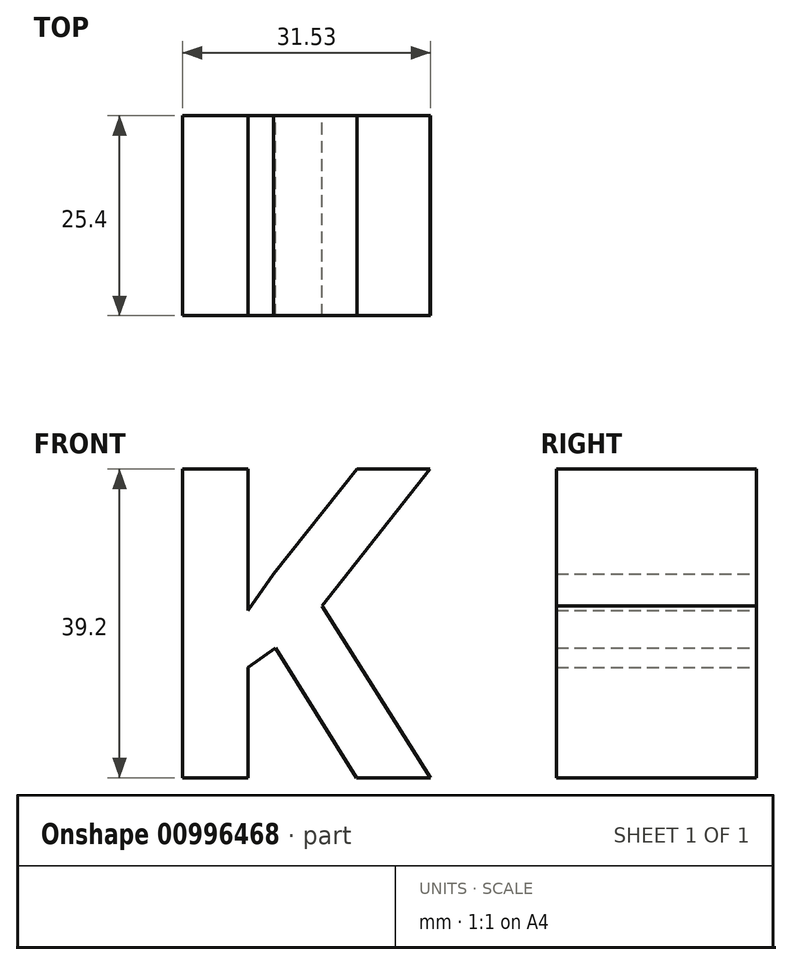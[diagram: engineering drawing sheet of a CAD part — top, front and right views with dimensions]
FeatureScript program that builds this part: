
annotation { "Feature Type Name" : "Feature", "Feature Type Description" : "" }
export const myFeature = defineFeature(function(context is Context, id is Id, definition is map)
    precondition{}
    {
        {
            var Q0;
            Q0=qCreatedBy(makeId("Front.planeOp"),FACE);
            var sketch = newSketch(context, id + "F0", { "sketchPlane" : qUnion([Q0])});
            skText(sketch, "E0", { "text": "K", "fontName": "OpenSans-Bold.ttf"});
            const initialGuessF0  = {"E0": [0, 0, 1, 0, 0.03953]};
            skSetInitialGuess(sketch, initialGuessF0);
            skSolve(sketch);
        }
        {
            var Q0;
            Q0=makeQuery(id+"F0.imprint","IMPRINT",FACE,{"disambiguationData":[TD([[makeQuery(id+"F0.imprint","IMPRINT",EDGE,{"derivedFrom":sQuery(id+"F0.wireOp",EDGE,"E0.sketch_text.stroke-0")}),-1.0]])]});
            extrude(context, id + "F1", {"entities" : qUnion([Q0]), "endBound" : BoundingType.SYMMETRIC, "depth" : 25.4 * mm, "offsetDistance" : 25.4 * mm});
        }
    });
